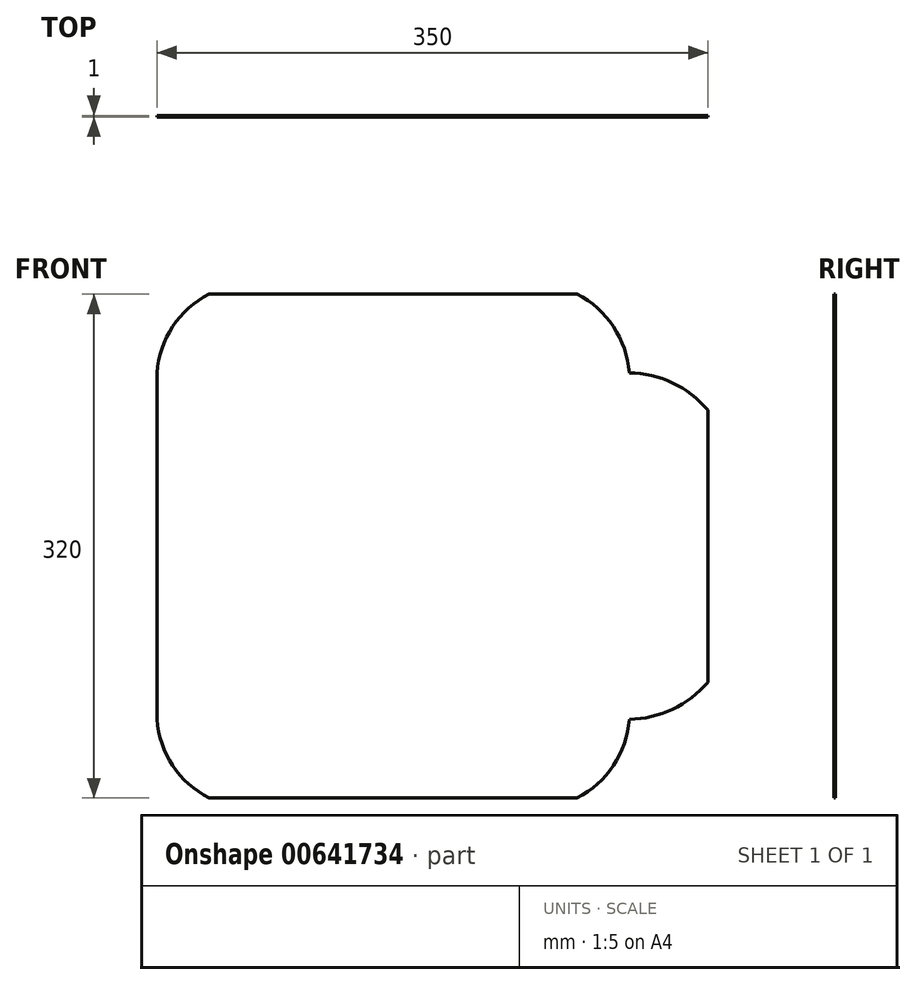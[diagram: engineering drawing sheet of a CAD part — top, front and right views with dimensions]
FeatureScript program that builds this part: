
annotation { "Feature Type Name" : "Feature", "Feature Type Description" : "" }
export const myFeature = defineFeature(function(context is Context, id is Id, definition is map)
    precondition{}
    {
        {
            var Q0;
            Q0=qCreatedBy(makeId("Front.planeOp"),FACE);
            var sketch = newSketch(context, id + "F0", { "sketchPlane" : qUnion([Q0])});
            skLineSegment(sketch, "E0.bottom", {"start": v(-147.82, 104.24) * mm, "end": v(85.8, 104.24) * mm});
            skLineSegment(sketch, "E0.top", {"start": v(-147.82, -215.76) * mm, "end": v(85.8, -215.76) * mm});
            skLineSegment(sketch, "E0.left", {"start": v(-181, 54.24) * mm, "end": v(-181, -165.76) * mm});
            skLineSegment(sketch, "E1", {"start": v(119, -165.76) * mm, "end": v(-181, -165.76) * mm});
            skLineSegment(sketch, "E2", {"start": v(119, 54.24) * mm, "end": v(-181, 54.24) * mm});
            skLineSegment(sketch, "E3", {"start": v(119, 54.24) * mm, "end": v(119, -165.76) * mm});
            skPoint(sketch, "E4.orphan", {"position": v(-181, -55.76) * mm});
            skPoint(sketch, "E5.start.orphan", {"position": v(169, -55.76) * mm});
            skArc(sketch, "E6", {"start": v(-181, -165.76) * mm, "mid": v(-171, -195.13) * mm, "end": v(-147.82, -215.76) * mm});
            skArc(sketch, "E7.MirrorCS", {"start": v(119, -165.76) * mm, "mid": v(109, -195.13) * mm, "end": v(85.8, -215.76) * mm});
            skArc(sketch, "E8.MirrorCS", {"start": v(-181, 54.24) * mm, "mid": v(-171, 83.61) * mm, "end": v(-147.82, 104.24) * mm});
            skArc(sketch, "E9.MirrorCS", {"start": v(119, 54.24) * mm, "mid": v(109, 83.61) * mm, "end": v(85.8, 104.24) * mm});
            skArc(sketch, "E10", {"start": v(169, 30.68) * mm, "mid": v(146.55, 47.88) * mm, "end": v(119, 54.24) * mm});
            skArc(sketch, "E11.MirrorCS", {"start": v(169, -142.2) * mm, "mid": v(146.55, -159.4) * mm, "end": v(119, -165.76) * mm});
            skPoint(sketch, "E12.orphan", {"position": v(-181, 104.24) * mm});
            skLineSegment(sketch, "E13.trimOffspring", {"start": v(169, 30.68) * mm, "end": v(169, -142.2) * mm});
            skPoint(sketch, "E14.orphan", {"position": v(169, -215.76) * mm});
            skPoint(sketch, "E15.orphan", {"position": v(-181, -215.76) * mm});
            skPoint(sketch, "E0.right.start.orphan", {"position": v(169, 104.24) * mm});
            skSolve(sketch);
        }
        {
            var Q0;
            Q0 = qSketchRegion(id + "F0", true);
            extrude(context, id + "F1", {"entities" : qUnion([Q0]), "depth" : 1 * mm, "offsetDistance" : 25 * mm});
        }
    });
